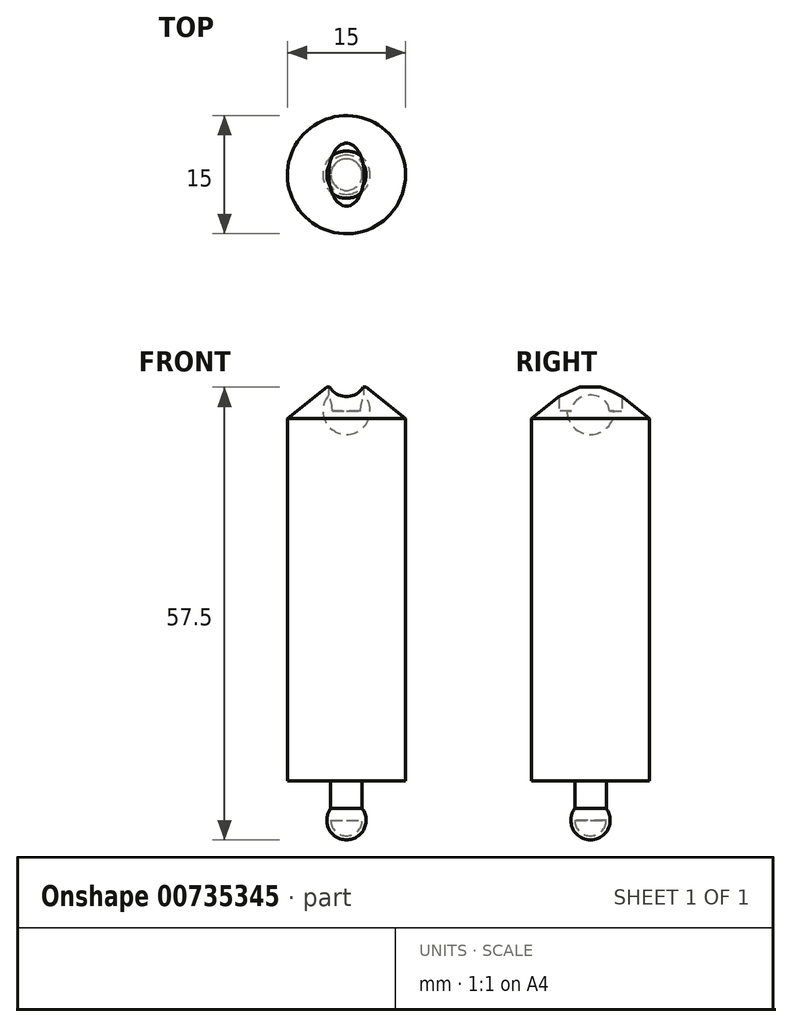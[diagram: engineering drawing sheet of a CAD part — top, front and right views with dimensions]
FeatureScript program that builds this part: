
annotation { "Feature Type Name" : "Feature", "Feature Type Description" : "" }
export const myFeature = defineFeature(function(context is Context, id is Id, definition is map)
    precondition{}
    {
        {
            var Q0;
            Q0=qCreatedBy(makeId("Top.planeOp"),FACE);
            var sketch = newSketch(context, id + "F0", { "sketchPlane" : qUnion([Q0])});
            skCircle(sketch, "E0", {"center": v(0, 0) * mm, "radius": 7.5 * mm});
            skSolve(sketch);
        }
        {
            var Q0;
            Q0 = qSketchRegion(id + "F0", true);
            extrude(context, id + "F1", {"entities" : qUnion([Q0]), "depth" : 50 * mm, "offsetDistance" : 25 * mm});
        }
        {
            var Q0;
            Q0=makeQuery(id+"F1.opExtrude","CAP_FACE",FACE,{"disambiguationData":[OSD([sQuery(id+"F0.wireOp",EDGE,"E0")])],"isStart":true});
            var sketch = newSketch(context, id + "F2", { "sketchPlane" : qUnion([Q0])});
            skCircle(sketch, "E1", {"center": v(0, 0) * mm, "radius": 2 * mm});
            skSolve(sketch);
        }
        {
            var Q0;
            Q0 = qSketchRegion(id + "F2", true);
            extrude(context, id + "F3", {"entities" : qUnion([Q0]), "operationType" : NewBodyOperationType.ADD, "depth" : 5 * mm, "offsetDistance" : 25 * mm});
        }
        {
            var Q0;
            Q0=makeQuery(id+"F3.opExtrude","CAP_FACE",FACE,{"disambiguationData":[OSD([sQuery(id+"F2.wireOp",EDGE,"E1")])],"isStart":false});
            var sketch = newSketch(context, id + "F4", { "sketchPlane" : qUnion([Q0])});
            skCircle(sketch, "E2", {"center": v(0, 0) * mm, "radius": 2.5 * mm});
            skLineSegment(sketch, "E3", {"start": v(0, 2.5) * mm, "end": v(0, -2.5) * mm});
            skSolve(sketch);
        }
        {
            var Q0;
            {var subQ0=sQuery(id+"F4.wireOp",EDGE,"E3");var subQ1=sQuery(id+"F4.wireOp",EDGE,"E2");var subQ2=makeQuery(id+"F4.imprint","INTERSECT",VERTEX,{"disambiguationData":[OD(0.0)],"derivedFrom":[subQ1,subQ0]});Q0=makeQuery(id+"F4.imprint","IMPRINT",FACE,{"disambiguationData":[TD([[makeQuery(id+"F4.imprint","IMPRINT",EDGE,{"disambiguationData":[TD([[subQ2,-1.0]])],"derivedFrom":subQ1}),1.0]])]});}
            var Q1;
            Q1=sQuery(id+"F4.wireOp",EDGE,"E3");
            revolve(context, id + "F5", {"operationType" : NewBodyOperationType.ADD, "surfaceOperationType" : NewSurfaceOperationType.NEW, "entities" : qUnion([Q0]), "axis" : qUnion([Q1]), "revolveType" : RevolveType.FULL});
        }
        {
            var Q0;
            Q0=makeQuery(id+"F1.opExtrude","CAP_FACE",FACE,{"disambiguationData":[OSD([sQuery(id+"F0.wireOp",EDGE,"E0")])],"isStart":false});
            var sketch = newSketch(context, id + "F6", { "sketchPlane" : qUnion([Q0])});
            skEllipse(sketch, "E4", {"center": v(0, 0) * mm, "majorRadius": 4 * mm, "minorRadius": 2.25 * mm, "majorAxis": v(0, 1)});
            skSolve(sketch);
        }
        {
            var Q0;
            Q0 = qSketchRegion(id + "F6", true);
            extrude(context, id + "F7", {"entities" : qUnion([Q0]), "operationType" : NewBodyOperationType.REMOVE, "oppositeDirection" : true, "depth" : 3 * mm, "offsetDistance" : 25 * mm});
        }
        {
            var Q0;
            Q0=makeQuery(id+"F7.boolean.opBoolean","COPY",FACE,{"derivedFrom":makeQuery(id+"F7.opExtrude","CAP_FACE",FACE,{"disambiguationData":[OSD([sQuery(id+"F6.wireOp",EDGE,"E4")])],"isStart":false})});
            var sketch = newSketch(context, id + "F8", { "sketchPlane" : qUnion([Q0])});
            skCircle(sketch, "E5", {"center": v(0, 0) * mm, "radius": 3 * mm});
            skLineSegment(sketch, "E6", {"start": v(0, 3) * mm, "end": v(0, -3) * mm});
            skPoint(sketch, "E6.endSnap0", {"position": v(0, 4) * mm});
            skSolve(sketch);
        }
        {
            var Q0;
            {var subQ0=sQuery(id+"F8.wireOp",EDGE,"E5");var subQ1=makeQuery(id+"F7.boolean.opBoolean","COPY",EDGE,{"derivedFrom":makeQuery(id+"F7.opExtrude","CAP_EDGE",EDGE,{"disambiguationData":[OSD([sQuery(id+"F6.wireOp",EDGE,"E4")])],"isStart":false})});var subQ2=makeQuery(id+"F8.imprint","INTERSECT",VERTEX,{"disambiguationData":[OD(1.0)],"derivedFrom":[subQ1,subQ0]});Q0=makeQuery(id+"F8.imprint","IMPRINT",FACE,{"disambiguationData":[TD([[makeQuery(id+"F8.imprint","IMPRINT",EDGE,{"disambiguationData":[TD([[subQ2,-1.0]])],"derivedFrom":subQ0}),1.0]])]});}
            var Q1;
            {var subQ0=sQuery(id+"F8.wireOp",EDGE,"E6");Q1=makeQuery(id+"F8.imprint","IMPRINT",FACE,{"disambiguationData":[TD([[makeQuery(id+"F8.imprint","IMPRINT",EDGE,{"derivedFrom":subQ0}),-1.0]])]});}
            var Q2;
            Q2=sQuery(id+"F8.wireOp",EDGE,"E6");
            revolve(context, id + "F9", {"operationType" : NewBodyOperationType.REMOVE, "surfaceOperationType" : NewSurfaceOperationType.NEW, "entities" : qUnion([Q0, Q1]), "axis" : qUnion([Q2]), "revolveType" : RevolveType.FULL, "oppositeDirection" : true});
        }
        {
            var Q0;
            Q0=makeQuery(id+"F1.opExtrude","CAP_EDGE",EDGE,{"disambiguationData":[OSD([sQuery(id+"F0.wireOp",EDGE,"E0")])],"isStart":false});
            chamfer(context, id + "F10", {"entities" : qUnion([Q0]), "chamferType" : ChamferType.TWO_OFFSETS, "width1" : 5 * mm, "oppositeDirection" : false, "width2" : 4 * mm, "tangentPropagation" : true});
        }
    });
